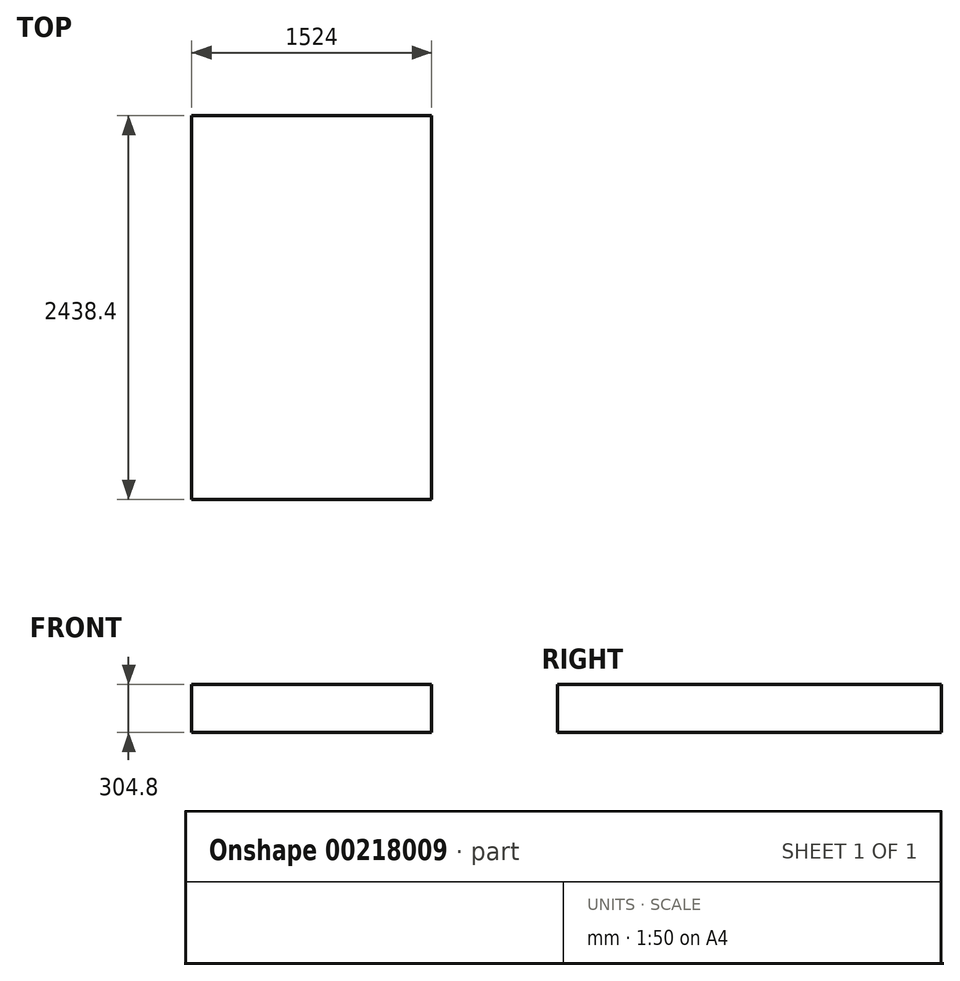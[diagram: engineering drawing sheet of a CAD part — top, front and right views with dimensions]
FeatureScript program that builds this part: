
annotation { "Feature Type Name" : "Feature", "Feature Type Description" : "" }
export const myFeature = defineFeature(function(context is Context, id is Id, definition is map)
    precondition{}
    {
        {
            var Q0;
            Q0=qCreatedBy(makeId("Top.planeOp"),FACE);
            var sketch = newSketch(context, id + "F0", { "sketchPlane" : qUnion([Q0])});
            skLineSegment(sketch, "E0.bottom", {"start": v(0, 0) * mm, "end": v(1524, 0) * mm});
            skLineSegment(sketch, "E0.top", {"start": v(0, 2438.4) * mm, "end": v(1524, 2438.4) * mm});
            skLineSegment(sketch, "E0.left", {"start": v(0, 0) * mm, "end": v(0, 2438.4) * mm});
            skLineSegment(sketch, "E0.right", {"start": v(1524, 0) * mm, "end": v(1524, 2438.4) * mm});
            skSolve(sketch);
        }
        {
            var Q0;
            Q0 = qSketchRegion(id + "F0", true);
            extrude(context, id + "F1", {"entities" : qUnion([Q0]), "depth" : 304.8 * mm});
        }
    });
